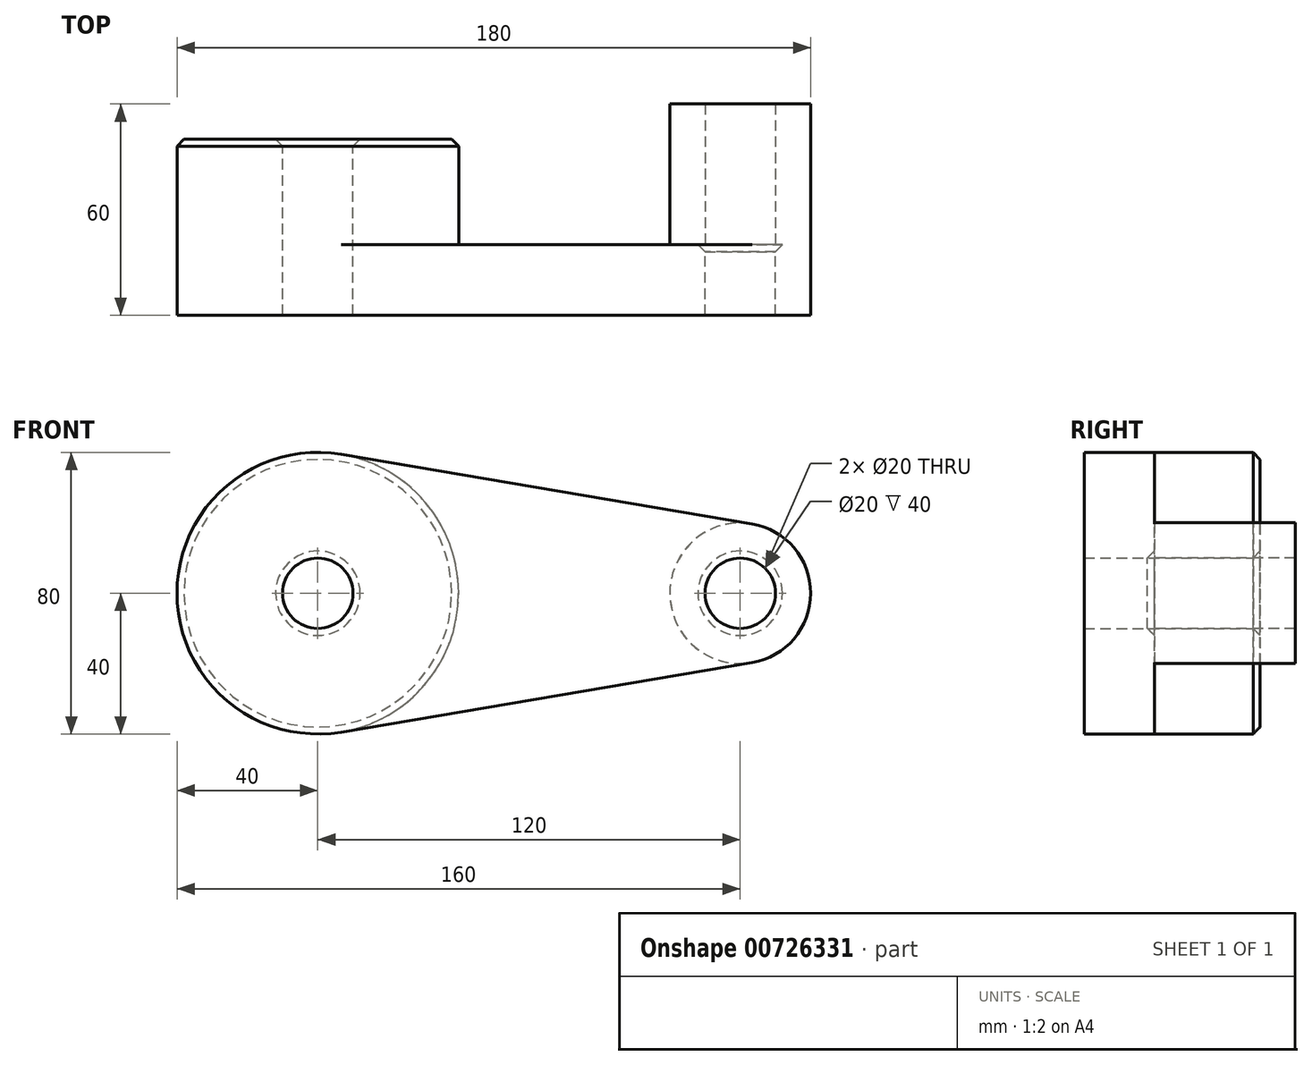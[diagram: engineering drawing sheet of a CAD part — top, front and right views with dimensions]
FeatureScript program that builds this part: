
annotation { "Feature Type Name" : "Feature", "Feature Type Description" : "" }
export const myFeature = defineFeature(function(context is Context, id is Id, definition is map)
    precondition{}
    {
        {
            var Q0;
            Q0=qCreatedBy(makeId("Front.planeOp"),FACE);
            var sketch = newSketch(context, id + "F0", { "sketchPlane" : qUnion([Q0])});
            skCircle(sketch, "E0", {"center": v(0, 0) * mm, "radius": 40 * mm});
            skCircle(sketch, "E1", {"center": v(120, 0) * mm, "radius": 20 * mm});
            skLineSegment(sketch, "E2", {"start": v(6.67, 39.44) * mm, "end": v(123.33, 19.72) * mm});
            skLineSegment(sketch, "E3", {"start": v(6.67, -39.44) * mm, "end": v(123.33, -19.72) * mm});
            skCircle(sketch, "E4", {"center": v(0, 0) * mm, "radius": 10 * mm});
            skCircle(sketch, "E5", {"center": v(120, 0) * mm, "radius": 10 * mm});
            skSolve(sketch);
        }
        {
            var Q0;
            {var subQ0=sQuery(id+"F0.wireOp",EDGE,"E2");Q0=makeQuery(id+"F0.imprint","IMPRINT",FACE,{"disambiguationData":[TD([[makeQuery(id+"F0.imprint","IMPRINT",EDGE,{"derivedFrom":subQ0}),-1.0]])]});}
            var Q1;
            Q1=makeQuery(id+"F0.imprint","IMPRINT",FACE,{"disambiguationData":[TD([[makeQuery(id+"F0.imprint","IMPRINT",EDGE,{"derivedFrom":sQuery(id+"F0.wireOp",EDGE,"E5")}),-1.0]])]});
            var Q2;
            Q2=makeQuery(id+"F0.imprint","IMPRINT",FACE,{"disambiguationData":[TD([[makeQuery(id+"F0.imprint","IMPRINT",EDGE,{"derivedFrom":sQuery(id+"F0.wireOp",EDGE,"E4")}),-1.0]])]});
            extrude(context, id + "F1", {"entities" : qUnion([Q0, Q1, Q2]), "depth" : 20 * mm, "offsetDistance" : 25 * mm});
        }
        {
            var Q0;
            Q0=makeQuery(id+"F0.imprint","IMPRINT",FACE,{"disambiguationData":[TD([[makeQuery(id+"F0.imprint","IMPRINT",EDGE,{"derivedFrom":sQuery(id+"F0.wireOp",EDGE,"E4")}),-1.0]])]});
            extrude(context, id + "F2", {"entities" : qUnion([Q0]), "operationType" : NewBodyOperationType.ADD, "oppositeDirection" : true, "depth" : 30 * mm, "offsetDistance" : 25 * mm});
        }
        {
            var Q0;
            Q0=makeQuery(id+"F2.opExtrude","CAP_EDGE",EDGE,{"disambiguationData":[OSD([sQuery(id+"F0.wireOp",EDGE,"E4")])],"isStart":false});
            var Q1;
            Q1=makeQuery(id+"F2.opExtrude","CAP_EDGE",EDGE,{"disambiguationData":[OSD([sQuery(id+"F0.wireOp",EDGE,"E0")])],"isStart":false});
            var Q2;
            Q2=makeQuery(id+"F1.opExtrude","CAP_EDGE",EDGE,{"disambiguationData":[OSD([sQuery(id+"F0.wireOp",EDGE,"E5")])],"isStart":true});
            chamfer(context, id + "F3", {"entities" : qUnion([Q0, Q1, Q2]), "width" : 2 * mm, "tangentPropagation" : true});
        }
        {
            var Q0;
            Q0=makeQuery(id+"F0.imprint","IMPRINT",FACE,{"disambiguationData":[TD([[makeQuery(id+"F0.imprint","IMPRINT",EDGE,{"derivedFrom":sQuery(id+"F0.wireOp",EDGE,"E5")}),-1.0]])]});
            extrude(context, id + "F4", {"entities" : qUnion([Q0]), "operationType" : NewBodyOperationType.ADD, "oppositeDirection" : true, "depth" : 40 * mm, "offsetDistance" : 25 * mm});
        }
    });
